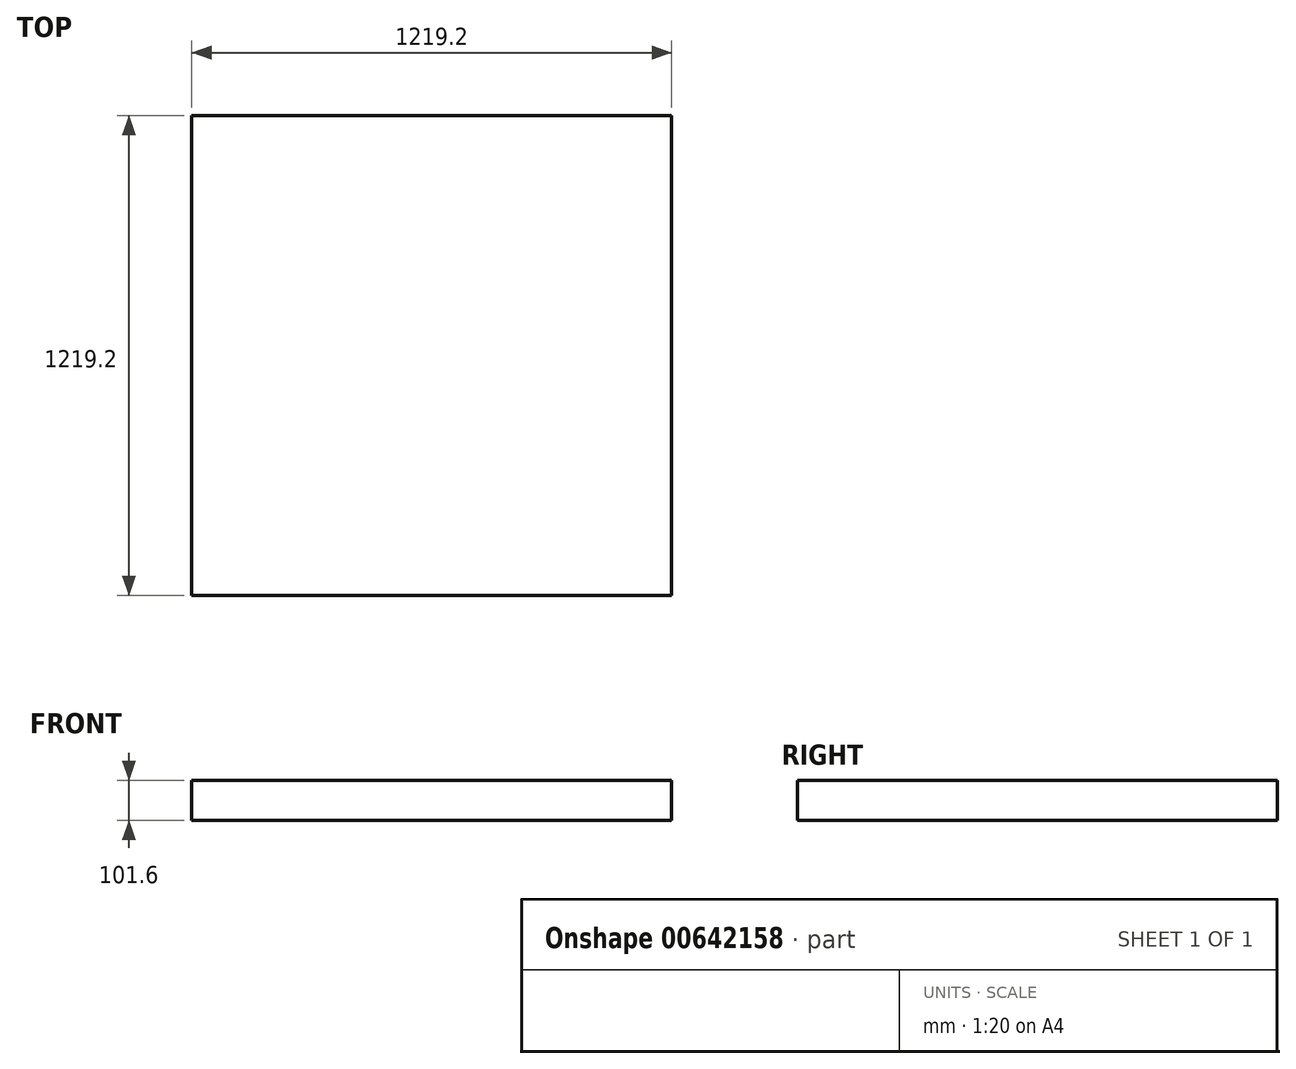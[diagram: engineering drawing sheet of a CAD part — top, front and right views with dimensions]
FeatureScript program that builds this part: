
annotation { "Feature Type Name" : "Feature", "Feature Type Description" : "" }
export const myFeature = defineFeature(function(context is Context, id is Id, definition is map)
    precondition{}
    {
        {
            var Q0;
            Q0=qCreatedBy(makeId("Top.planeOp"),FACE);
            var sketch = newSketch(context, id + "F0", { "sketchPlane" : qUnion([Q0])});
            skLineSegment(sketch, "E0.bottom", {"start": v(0, 0) * mm, "end": v(-1219.2, 0) * mm});
            skLineSegment(sketch, "E0.top", {"start": v(0, 1219.2) * mm, "end": v(-1219.2, 1219.2) * mm});
            skLineSegment(sketch, "E0.left", {"start": v(0, 0) * mm, "end": v(0, 1219.2) * mm});
            skLineSegment(sketch, "E0.right", {"start": v(-1219.2, 0) * mm, "end": v(-1219.2, 1219.2) * mm});
            skSolve(sketch);
        }
        {
            var Q0;
            Q0=makeQuery(id+"F0.imprint","IMPRINT",FACE,{"disambiguationData":[TD([[makeQuery(id+"F0.imprint","IMPRINT",EDGE,{"derivedFrom":sQuery(id+"F0.wireOp",EDGE,"E0.bottom")}),-1.0]])]});
            extrude(context, id + "F1", {"entities" : qUnion([Q0]), "depth" : 101.6 * mm, "offsetDistance" : 25.4 * mm});
        }
        {
            var Q0;
            Q0=makeQuery(id+"F1.opExtrude","SWEPT_FACE",FACE,{"disambiguationData":[OSD([sQuery(id+"F0.wireOp",EDGE,"E0.left")])]});
            var sketch = newSketch(context, id + "F2", { "sketchPlane" : qUnion([Q0])});
            skCircle(sketch, "E1", {"center": v(963.85, 53.59) * mm, "radius": 12.7 * mm});
            skCircle(sketch, "E2", {"center": v(996.5, 53.59) * mm, "radius": 13 * mm});
            skSolve(sketch);
        }
        {
            var Q0;
            Q0=sQuery(id+"F2.wireOp",EDGE,"E2");
            var Q1;
            Q1=sQuery(id+"F2.wireOp",EDGE,"E1");
            extrude(context, id + "F3", {"bodyType" : ToolBodyType.SURFACE, "surfaceEntities" : qUnion([Q0, Q1]), "depth" : 25.4 * mm, "offsetDistance" : 25.4 * mm});
        }
    });
